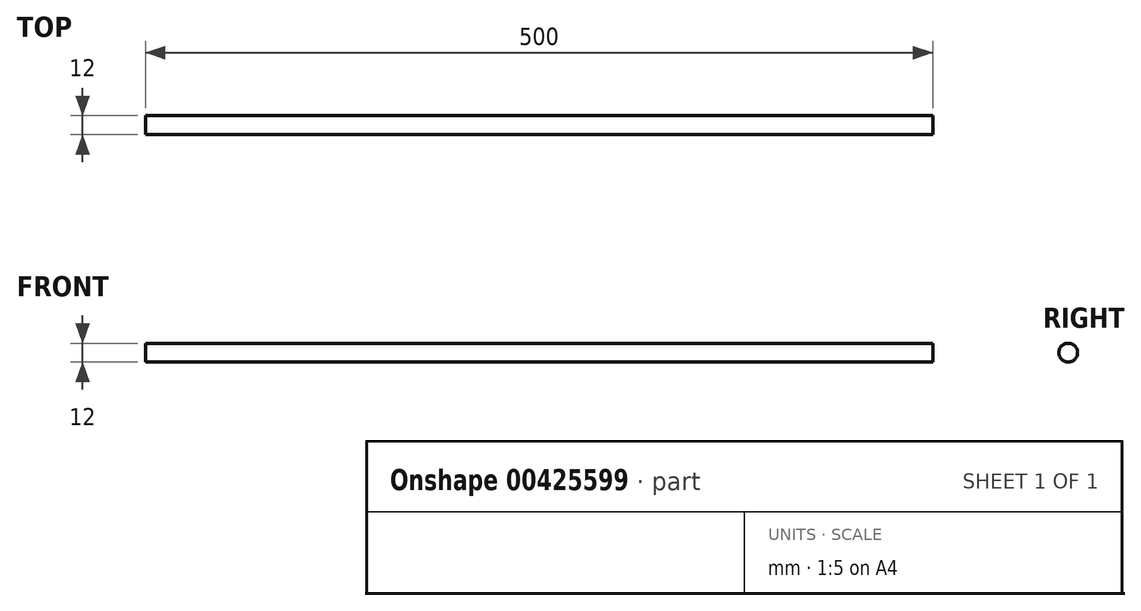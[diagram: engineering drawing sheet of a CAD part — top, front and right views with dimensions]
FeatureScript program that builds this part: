
annotation { "Feature Type Name" : "Feature", "Feature Type Description" : "" }
export const myFeature = defineFeature(function(context is Context, id is Id, definition is map)
    precondition{}
    {
        {
            var Q0;
            Q0=qCreatedBy(makeId("Right.planeOp"),FACE);
            var sketch = newSketch(context, id + "F0", { "sketchPlane" : qUnion([Q0])});
            skCircle(sketch, "E0", {"center": v(0, 0) * mm, "radius": 6 * mm});
            skSolve(sketch);
        }
        {
            var Q0;
            Q0 = qSketchRegion(id + "F0", true);
            extrude(context, id + "F1", {"entities" : qUnion([Q0]), "depth" : 500 * mm});
        }
    });
